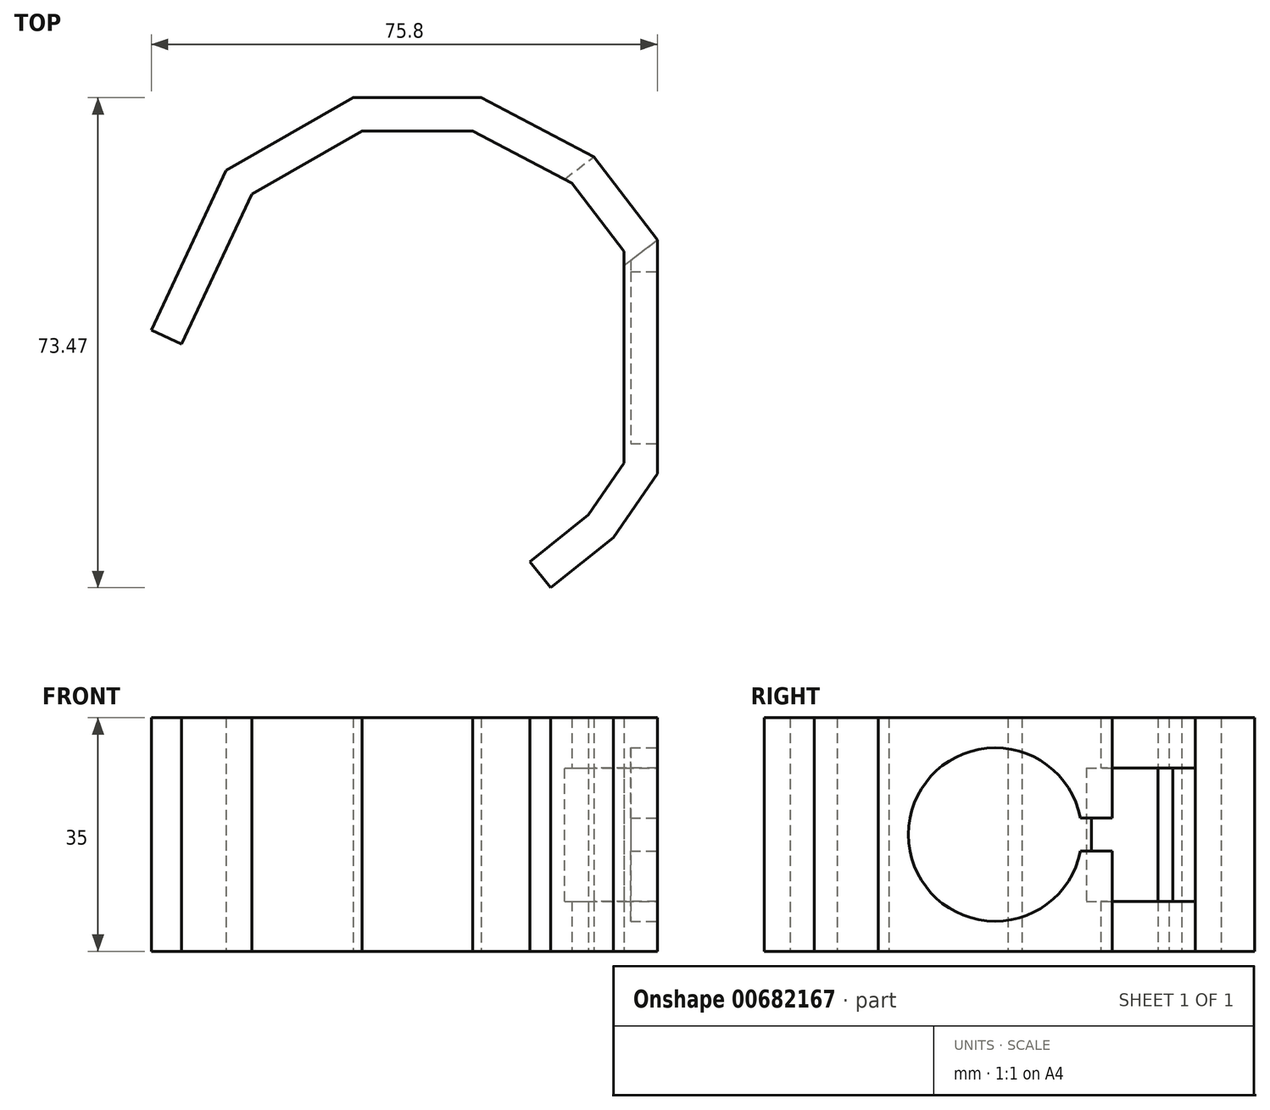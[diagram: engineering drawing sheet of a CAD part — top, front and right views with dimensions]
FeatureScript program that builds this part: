
annotation { "Feature Type Name" : "Feature", "Feature Type Description" : "" }
export const myFeature = defineFeature(function(context is Context, id is Id, definition is map)
    precondition{}
    {
        {
            var Q0;
            Q0=qCreatedBy(makeId("Top.planeOp"),FACE);
            var sketch = newSketch(context, id + "F0", { "sketchPlane" : qUnion([Q0])});
            skLineSegment(sketch, "E0", {"start": v(0, 0) * mm, "end": v(0, -35) * mm});
            skLineSegment(sketch, "E1", {"start": v(0, -35) * mm, "end": v(-6.6, -44.62) * mm});
            skLineSegment(sketch, "E2", {"start": v(-6.6, -44.62) * mm, "end": v(-15.99, -52.13) * mm});
            skLineSegment(sketch, "E3", {"start": v(0, 0) * mm, "end": v(-9.51, 12.47) * mm});
            skLineSegment(sketch, "E4", {"start": v(-9.51, 12.47) * mm, "end": v(-26.42, 21.34) * mm});
            skCircle(sketch, "E5", {"center": v(-36, -17.5) * mm, "radius": 40 * mm, "construction": true});
            skLineSegment(sketch, "E6", {"start": v(-26.42, 21.34) * mm, "end": v(-45.58, 21.34) * mm});
            skLineSegment(sketch, "E7", {"start": v(-45.58, 21.34) * mm, "end": v(-64.6, 10.47) * mm});
            skLineSegment(sketch, "E8", {"start": v(-64.6, 10.47) * mm, "end": v(-75.8, -13.47) * mm});
            skLineSegment(sketch, "E9.0", {"start": v(-60.74, 6.91) * mm, "end": v(-71.27, -15.59) * mm});
            skLineSegment(sketch, "E9.1", {"start": v(-44.25, 16.34) * mm, "end": v(-60.74, 6.91) * mm});
            skLineSegment(sketch, "E9.2", {"start": v(-27.65, 16.34) * mm, "end": v(-44.25, 16.34) * mm});
            skLineSegment(sketch, "E9.3", {"start": v(-12.81, 8.56) * mm, "end": v(-27.65, 16.34) * mm});
            skLineSegment(sketch, "E9.4", {"start": v(-10.3, -41.18) * mm, "end": v(-19.11, -48.23) * mm});
            skLineSegment(sketch, "E9.5", {"start": v(-5, -33.45) * mm, "end": v(-10.3, -41.18) * mm});
            skLineSegment(sketch, "E9.6", {"start": v(-5, -1.69) * mm, "end": v(-5, -33.45) * mm});
            skLineSegment(sketch, "E9.7", {"start": v(-5, -1.69) * mm, "end": v(-12.81, 8.56) * mm});
            skLineSegment(sketch, "E10", {"start": v(-75.8, -13.47) * mm, "end": v(-71.27, -15.59) * mm});
            skLineSegment(sketch, "E11", {"start": v(-19.11, -48.23) * mm, "end": v(-15.99, -52.13) * mm});
            skSolve(sketch);
        }
        {
            var Q0;
            Q0=makeQuery(id+"F0.imprint","IMPRINT",FACE,{"disambiguationData":[TD([[makeQuery(id+"F0.imprint","IMPRINT",EDGE,{"derivedFrom":sQuery(id+"F0.wireOp",EDGE,"E0")}),-1.0]])]});
            extrude(context, id + "F1", {"entities" : qUnion([Q0]), "depth" : 35 * mm, "offsetDistance" : 25 * mm});
        }
        {
            var Q0;
            Q0=makeQuery(id+"F1.opExtrude","SWEPT_BODY",BODY,{"disambiguationData":[OSD([sQuery(id+"F0.wireOp",EDGE,"E0"),sQuery(id+"F0.wireOp",EDGE,"E1"),sQuery(id+"F0.wireOp",EDGE,"E2"),sQuery(id+"F0.wireOp",EDGE,"E3"),sQuery(id+"F0.wireOp",EDGE,"E4"),sQuery(id+"F0.wireOp",EDGE,"E6"),sQuery(id+"F0.wireOp",EDGE,"E7"),sQuery(id+"F0.wireOp",EDGE,"E8"),sQuery(id+"F0.wireOp",EDGE,"E9.0"),sQuery(id+"F0.wireOp",EDGE,"E9.1"),sQuery(id+"F0.wireOp",EDGE,"E9.2"),sQuery(id+"F0.wireOp",EDGE,"E9.3"),sQuery(id+"F0.wireOp",EDGE,"E9.4"),sQuery(id+"F0.wireOp",EDGE,"E9.5"),sQuery(id+"F0.wireOp",EDGE,"E9.6"),sQuery(id+"F0.wireOp",EDGE,"E9.7"),sQuery(id+"F0.wireOp",EDGE,"E10"),sQuery(id+"F0.wireOp",EDGE,"E11")])]});
            transform(context, id + "F2", {"entities" : qUnion([Q0]), "transformType" : TransformType.TRANSLATION_3D, "dx" : 0 * mm, "dy" : 0 * mm, "dz" : 0 * mm, "makeCopy" : true});
        }
        {
            var Q0;
            Q0=makeQuery(id+"F2.opPattern","COPY",FACE,{"derivedFrom":makeQuery(id+"F1.opExtrude","SWEPT_FACE",FACE,{"disambiguationData":[OSD([sQuery(id+"F0.wireOp",EDGE,"E0")])]}),"instanceName":"1"});
            var sketch = newSketch(context, id + "F3", { "sketchPlane" : qUnion([Q0])});
            skLineSegment(sketch, "E12", {"start": v(0, 17.5) * mm, "end": v(-35, 17.5) * mm, "construction": true});
            skArc(sketch, "E13", {"start": v(-4.74, 20) * mm, "mid": v(-30.5, 17.5) * mm, "end": v(-4.74, 15) * mm});
            skLineSegment(sketch, "E14", {"start": v(0, 15) * mm, "end": v(-4.74, 15) * mm});
            skLineSegment(sketch, "E15", {"start": v(0, 20) * mm, "end": v(-4.74, 20) * mm});
            skLineSegment(sketch, "E16", {"start": v(0, 15) * mm, "end": v(0, 20) * mm});
            skSolve(sketch);
        }
        {
            var Q0;
            Q0 = qSketchRegion(id + "F3", true);
            extrude(context, id + "F4", {"entities" : qUnion([Q0]), "operationType" : NewBodyOperationType.REMOVE, "oppositeDirection" : true, "depth" : 4 * mm, "offsetDistance" : 25 * mm});
        }
        {
            var Q0;
            Q0=makeQuery(id+"F2.opPattern","COPY",FACE,{"derivedFrom":makeQuery(id+"F1.opExtrude","SWEPT_FACE",FACE,{"disambiguationData":[OSD([sQuery(id+"F0.wireOp",EDGE,"E3")])]}),"instanceName":"1"});
            var sketch = newSketch(context, id + "F5", { "sketchPlane" : qUnion([Q0])});
            skLineSegment(sketch, "E17", {"start": v(0, 17.5) * mm, "end": v(0, 7.5) * mm});
            skLineSegment(sketch, "E18", {"start": v(0, 17.5) * mm, "end": v(0, 27.5) * mm});
            skLineSegment(sketch, "E19", {"start": v(0, 27.5) * mm, "end": v(15.68, 27.5) * mm});
            skLineSegment(sketch, "E20", {"start": v(0, 7.5) * mm, "end": v(15.68, 7.5) * mm});
            skLineSegment(sketch, "E21", {"start": v(15.68, 7.5) * mm, "end": v(15.68, 27.5) * mm});
            skSolve(sketch);
        }
        {
            var Q0;
            {var subQ4=sQuery(id+"F5.wireOp",EDGE,"E19");Q0=makeQuery(id+"F5.imprint","IMPRINT",FACE,{"disambiguationData":[TD([[makeQuery(id+"F5.imprint","IMPRINT",EDGE,{"derivedFrom":subQ4}),-1.0]])]});}
            extrude(context, id + "F6", {"entities" : qUnion([Q0]), "operationType" : NewBodyOperationType.REMOVE, "endBound" : BoundingType.THROUGH_ALL, "oppositeDirection" : true, "depth" : 25 * mm, "offsetDistance" : 25 * mm});
        }
    });
